# Revit family: Bleacher-Telescopic-Hussey-MAXAM-Wall_Attached
name_source: partatom
category: Specialty Equipment
units: mm (PartAtom-declared; Revit-internal decimal feet)

## family parameters
Always vertical = Yes
Classification Number = 23.40.50.34.14
Cut with Voids When Loaded = No
Enable Cutting in Views = No
Maintain Annotation Orientation = No
Part Type = Normal
Room Calculation Point = No
Round Connector Dimension = Use Diameter
Shared = No
Work Plane-Based = No

## types (1)
- 24" Row, 11 5/8" Rise
    Assembly Code = E1020900
    BIM Version = v3.1
    Bank Length Increment = 18'' Typical Increments
    Bank Length Maximum = 25'-6''
    Bank Length Minimum = 9'-0''
    Bleacher Deck Material = Hussey - Plywood - 001 Natural - Bleacher Decking
    CSI MasterFormat = 12 66 00
    Courtside XC12 Note = Not available for 22'' Row Spacing
    Default Elevation = 0"
    Description = MAXAM Telescopic Gym Bleacher Bank - Wall Attached
    End Rail Color = Hussey - Bleacher Rail Color
    Front Closure Material = Hussey - Galvanized Steel
    Manufacturer = Hussey Seating Company
    Model = MAXAM
    Nose Beam Material = Hussey - Galvanized Steel
    Product Page URL = http://www.husseyseating.com
    Riser Material = Hussey - Galvanized Steel
    Row Rise = 11 5/8"
    Row Rise Constraint = 2
    Row Rise Note = Do Not Change Row Rise Constraint
    Row Spacing = 2' - 0"
    Row Spacing Constraint = 3
    Row Spacing Note = Do Not Change Row Spacing Constraint
    Seat Type = Bleacher Seat : Courtside XC10
    Type Comments = Bleacher Bank
    URL = http://www.husseyseating.com

## geometry (parser evidence)
native form markers: Blend x24, Sweep x14
no freeform markers — native parametric forms only
